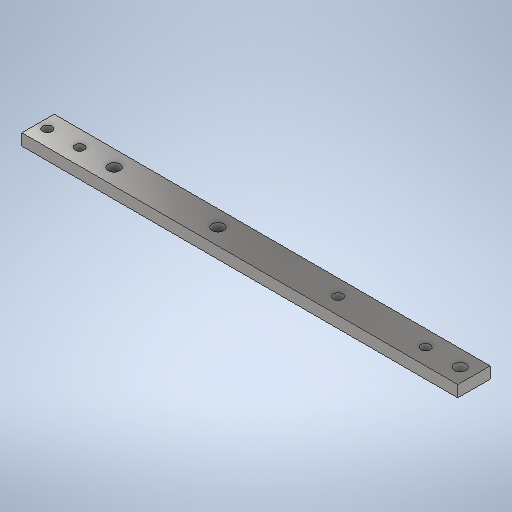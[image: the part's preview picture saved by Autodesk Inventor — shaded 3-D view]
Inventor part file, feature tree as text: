
AUTODESK INVENTOR PART (.ipt)
format: ipt  version: 2025.1 (Build 291241000, 241)  size: 277,504 bytes
history: native  units: mm
features: sketch x3, hole x2, extrude x1
ambient origin geometry x8: Origin, YZ Plane, XZ Plane, XY Plane, X Axis, Y Axis, Z Axis, Center Point
bodies: Solid1 (feature_tree)
feature tree (6):
  extrude  "Extrusion1"  Depth=189.0mm
  hole  "Hole1"  [1 undecoded]
  hole  "Hole2"  [1 undecoded]
  sketch  "Sketch1"  dims[d0=14.0mm d1=189.0mm]
  sketch  "Sketch2"  dims[d2=5.0mm d3=0.0mm d4=6.0mm]
  sketch  "Sketch3"  dims[d5=7.0mm d6=105.0mm d7=45.0mm d8=5.0mm d9=6.0mm d10=4.0mm d11=2.0mm d12=90.0deg d13=3.5mm d14=0.0mm d15=4.0mm d16=0.5mm d17=4.0mm d18=2.0mm d19=90.0deg d20=8.0mm d21=0.0mm d22=7.0mm d23=15.0mm d24=38.0mm d25=15.0mm d26=14.0mm]
note: 2 required parameter values undecoded (feature->parameter linkage not recoverable at this tier; creation-order binding heuristic only, values carry confidence <= 0.55)
